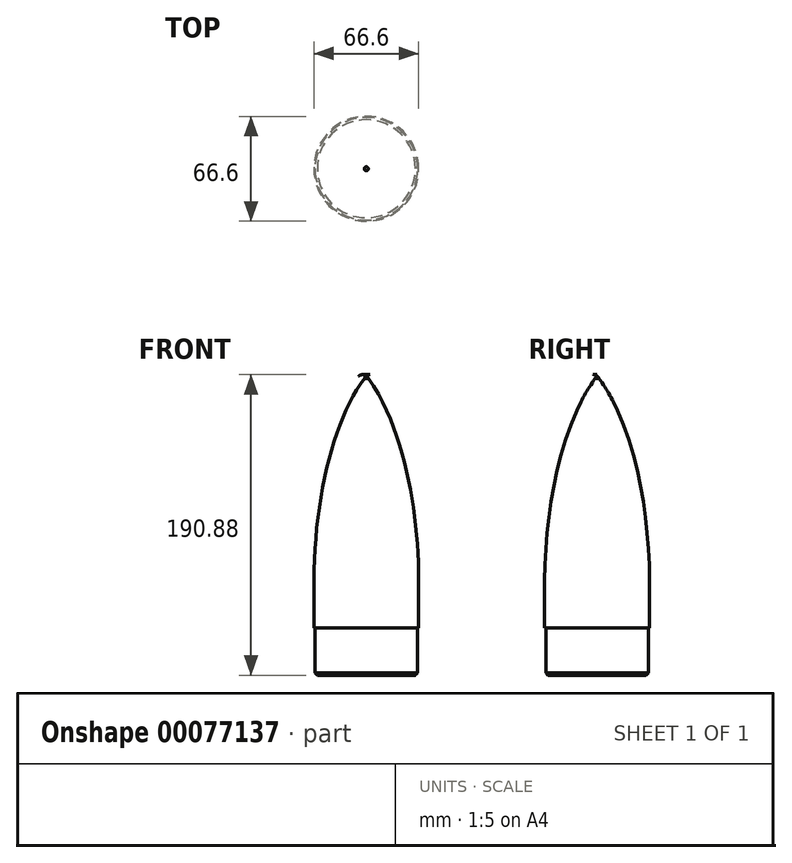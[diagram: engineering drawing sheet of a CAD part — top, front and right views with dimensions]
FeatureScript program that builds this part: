
annotation { "Feature Type Name" : "Feature", "Feature Type Description" : "" }
export const myFeature = defineFeature(function(context is Context, id is Id, definition is map)
    precondition{}
    {
        {
            var Q0;
            Q0=qCreatedBy(makeId("Front.planeOp"),FACE);
            var sketch = newSketch(context, id + "F0", { "sketchPlane" : qUnion([Q0])});
            skEllipticalArc(sketch, "E0", {});
            skLineSegment(sketch, "E1", {"start": v(0, -68.75) * mm, "end": v(0, 86.96) * mm});
            skLineSegment(sketch, "E2", {"start": v(0, -68.75) * mm, "end": v(0, -98.75) * mm});
            skPoint(sketch, "E3.orphan", {"position": v(0, 61.25) * mm});
            skLineSegment(sketch, "E4", {"start": v(-33.3, -68.75) * mm, "end": v(-33.3, -98.75) * mm});
            skLineSegment(sketch, "E5", {"start": v(-33.3, -98.75) * mm, "end": v(-32.6, -98.75) * mm});
            skArc(sketch, "E6", {"start": v(0, 61.25) * mm, "mid": v(-0.75, 60.5) * mm, "end": v(-1.28, 59.58) * mm});
            skLineSegment(sketch, "E7.top", {"start": v(-32.6, -128.79) * mm, "end": v(0, -128.79) * mm});
            skLineSegment(sketch, "E7.left", {"start": v(-32.6, -98.75) * mm, "end": v(-32.6, -128.79) * mm});
            skLineSegment(sketch, "E7.right", {"start": v(0, -98.75) * mm, "end": v(0, -128.79) * mm});
            const initialGuessF0  = {"E0": [0.026576005768498712, -0.06619656694530998, 0.016311071592733244, 0.9998669656226756, 0.14465189666781272, 0.059844210815227915, 0.5231788863908307, 1.5951998253377808]};
            skSetInitialGuess(sketch, initialGuessF0);
            skSolve(sketch);
        }
        {
            var Q0;
            Q0=makeQuery(id+"F0.imprint","IMPRINT",FACE,{"disambiguationData":[TD([[makeQuery(id+"F0.imprint","IMPRINT",EDGE,{"derivedFrom":sQuery(id+"F0.wireOp",EDGE,"E0")}),1.0]])]});
            var Q1;
            Q1=sQuery(id+"F0.wireOp",EDGE,"E1");
            revolve(context, id + "F1", {"entities" : qUnion([Q0]), "axis" : qUnion([Q1]), "revolveType" : RevolveType.FULL});
        }
        {
            var Q0;
            Q0=makeQuery(id+"F1.opRevolve","SWEPT_EDGE",EDGE,{"disambiguationData":[OSD([sQuery(id+"F0.wireOp",EDGE,"E7.top"),sQuery(id+"F0.wireOp",EDGE,"E7.left")])]});
            chamfer(context, id + "F2", {"entities" : qUnion([Q0]), "width" : 1.5 * mm, "tangentPropagation" : true});
        }
    });
